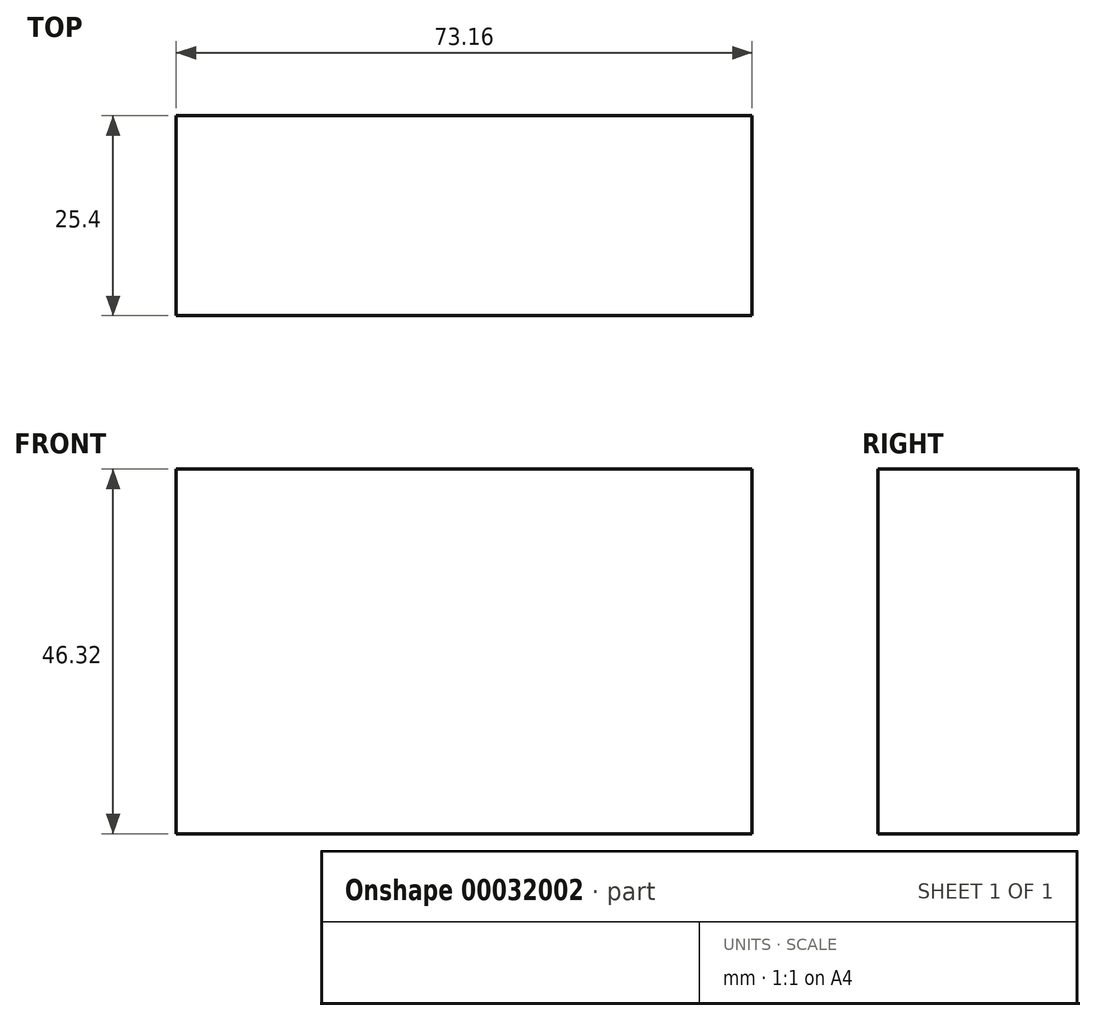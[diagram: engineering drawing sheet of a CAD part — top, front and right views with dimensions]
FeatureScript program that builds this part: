
annotation { "Feature Type Name" : "Feature", "Feature Type Description" : "" }
export const myFeature = defineFeature(function(context is Context, id is Id, definition is map)
    precondition{}
    {
        {
            var Q0;
            Q0=qCreatedBy(makeId("Front.planeOp"),FACE);
            var sketch = newSketch(context, id + "F0", { "sketchPlane" : qUnion([Q0])});
            skLineSegment(sketch, "E0.rect.bottom", {"start": v(36.58, -23.16) * mm, "end": v(-36.58, -23.16) * mm});
            skLineSegment(sketch, "E0.rect.top", {"start": v(36.58, 23.16) * mm, "end": v(-36.58, 23.16) * mm});
            skLineSegment(sketch, "E0.rect.left", {"start": v(36.58, -23.16) * mm, "end": v(36.58, 23.16) * mm});
            skLineSegment(sketch, "E0.rect.right", {"start": v(-36.58, -23.16) * mm, "end": v(-36.58, 23.16) * mm});
            skPoint(sketch, "E0.rect.middle", {"position": v(0, 0) * mm});
            skSolve(sketch);
        }
        {
            var Q0;
            Q0 = qSketchRegion(id + "F0", true);
            extrude(context, id + "F1", {"entities" : qUnion([Q0]), "depth" : 25.4 * mm});
        }
    });
